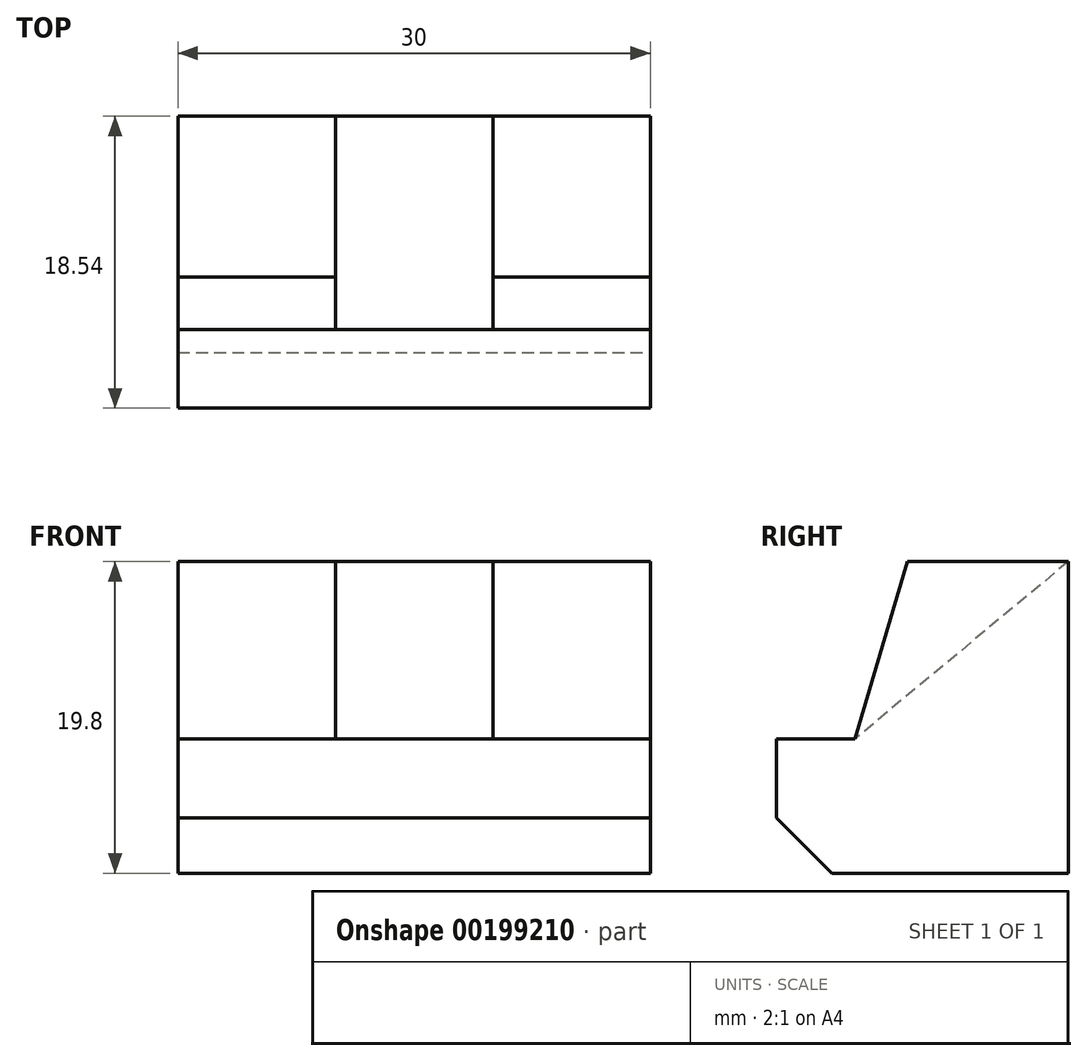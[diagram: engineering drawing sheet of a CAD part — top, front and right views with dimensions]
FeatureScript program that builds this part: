
annotation { "Feature Type Name" : "Feature", "Feature Type Description" : "" }
export const myFeature = defineFeature(function(context is Context, id is Id, definition is map)
    precondition{}
    {
        {
            var Q0;
            Q0=qCreatedBy(makeId("Right.planeOp"),FACE);
            var sketch = newSketch(context, id + "F0", { "sketchPlane" : qUnion([Q0])});
            skLineSegment(sketch, "E0", {"start": v(0, 0) * mm, "end": v(15, 0) * mm});
            skLineSegment(sketch, "E1", {"start": v(15, 0) * mm, "end": v(15, 19.8) * mm});
            skLineSegment(sketch, "E2", {"start": v(15, 19.8) * mm, "end": v(4.79, 19.8) * mm});
            skLineSegment(sketch, "E3", {"start": v(0, 0) * mm, "end": v(-3.54, 3.54) * mm});
            skLineSegment(sketch, "E4", {"start": v(-3.54, 3.54) * mm, "end": v(-3.54, 8.54) * mm});
            skLineSegment(sketch, "E5", {"start": v(-3.54, 8.54) * mm, "end": v(1.46, 8.54) * mm});
            skLineSegment(sketch, "E6", {"start": v(1.46, 8.54) * mm, "end": v(4.79, 19.8) * mm});
            skSolve(sketch);
        }
        {
            var Q0;
            Q0=makeQuery(id+"F0.imprint","IMPRINT",FACE,{"disambiguationData":[TD([[makeQuery(id+"F0.imprint","IMPRINT",EDGE,{"derivedFrom":sQuery(id+"F0.wireOp",EDGE,"E0")}),1.0]])]});
            extrude(context, id + "F1", {"entities" : qUnion([Q0]), "oppositeDirection" : true, "depth" : 15 * mm});
        }
        {
            var Q0;
            Q0=makeQuery(id+"F1.opExtrude","CAP_FACE",FACE,{"disambiguationData":[OSD([sQuery(id+"F0.wireOp",EDGE,"E0"),sQuery(id+"F0.wireOp",EDGE,"E1"),sQuery(id+"F0.wireOp",EDGE,"E2"),sQuery(id+"F0.wireOp",EDGE,"E3"),sQuery(id+"F0.wireOp",EDGE,"E4"),sQuery(id+"F0.wireOp",EDGE,"E5"),sQuery(id+"F0.wireOp",EDGE,"E6")])],"isStart":false});
            var sketch = newSketch(context, id + "F2", { "sketchPlane" : qUnion([Q0])});
            skLineSegment(sketch, "E7", {"start": v(-15, 19.8) * mm, "end": v(-1.46, 8.54) * mm});
            skSolve(sketch);
        }
        {
            var Q0;
            Q0=makeQuery(id+"F2.imprint","IMPRINT",FACE,{"disambiguationData":[TD([[makeQuery(id+"F2.imprint","IMPRINT",EDGE,{"derivedFrom":sQuery(id+"F2.wireOp",EDGE,"E7")}),1.0]])]});
            extrude(context, id + "F3", {"entities" : qUnion([Q0]), "operationType" : NewBodyOperationType.REMOVE, "oppositeDirection" : true, "depth" : 5 * mm});
        }
        {
            var Q0;
            Q0=makeQuery(id+"F1.opExtrude","CAP_EDGE",EDGE,{"disambiguationData":[OSD([sQuery(id+"F0.wireOp",EDGE,"E0")])],"isStart":false});
            cPoint(context, id + "F4", {"entities" : qUnion([Q0]), "parameter" : 0.5});
        }
        {
            var Q0;
            Q0=qCreatedBy(makeId("Right.planeOp"),FACE);
            var Q1;
            Q1 = qCreatedBy(id + "F4" ,VERTEX);
            cPlane(context, id + "F5", {"entities" : qUnion([Q0, Q1]), "cplaneType" : CPlaneType.PLANE_POINT, "offset" : 25 * mm, "width" : 150 * mm, "height" : 150 * mm});
        }
        {
            var Q0;
            Q0=makeQuery(id+"F1.opExtrude","SWEPT_BODY",BODY,{"disambiguationData":[OSD([sQuery(id+"F0.wireOp",EDGE,"E0"),sQuery(id+"F0.wireOp",EDGE,"E1"),sQuery(id+"F0.wireOp",EDGE,"E2"),sQuery(id+"F0.wireOp",EDGE,"E3"),sQuery(id+"F0.wireOp",EDGE,"E4"),sQuery(id+"F0.wireOp",EDGE,"E5"),sQuery(id+"F0.wireOp",EDGE,"E6")])]});
            var Q1;
            Q1=qCreatedBy(id+"F5.planeOp",FACE);
            mirror(context, id + "F6", {"operationType" : NewBodyOperationType.ADD, "entities" : qUnion([Q0]), "mirrorPlane" : qUnion([Q1])});
        }
    });
